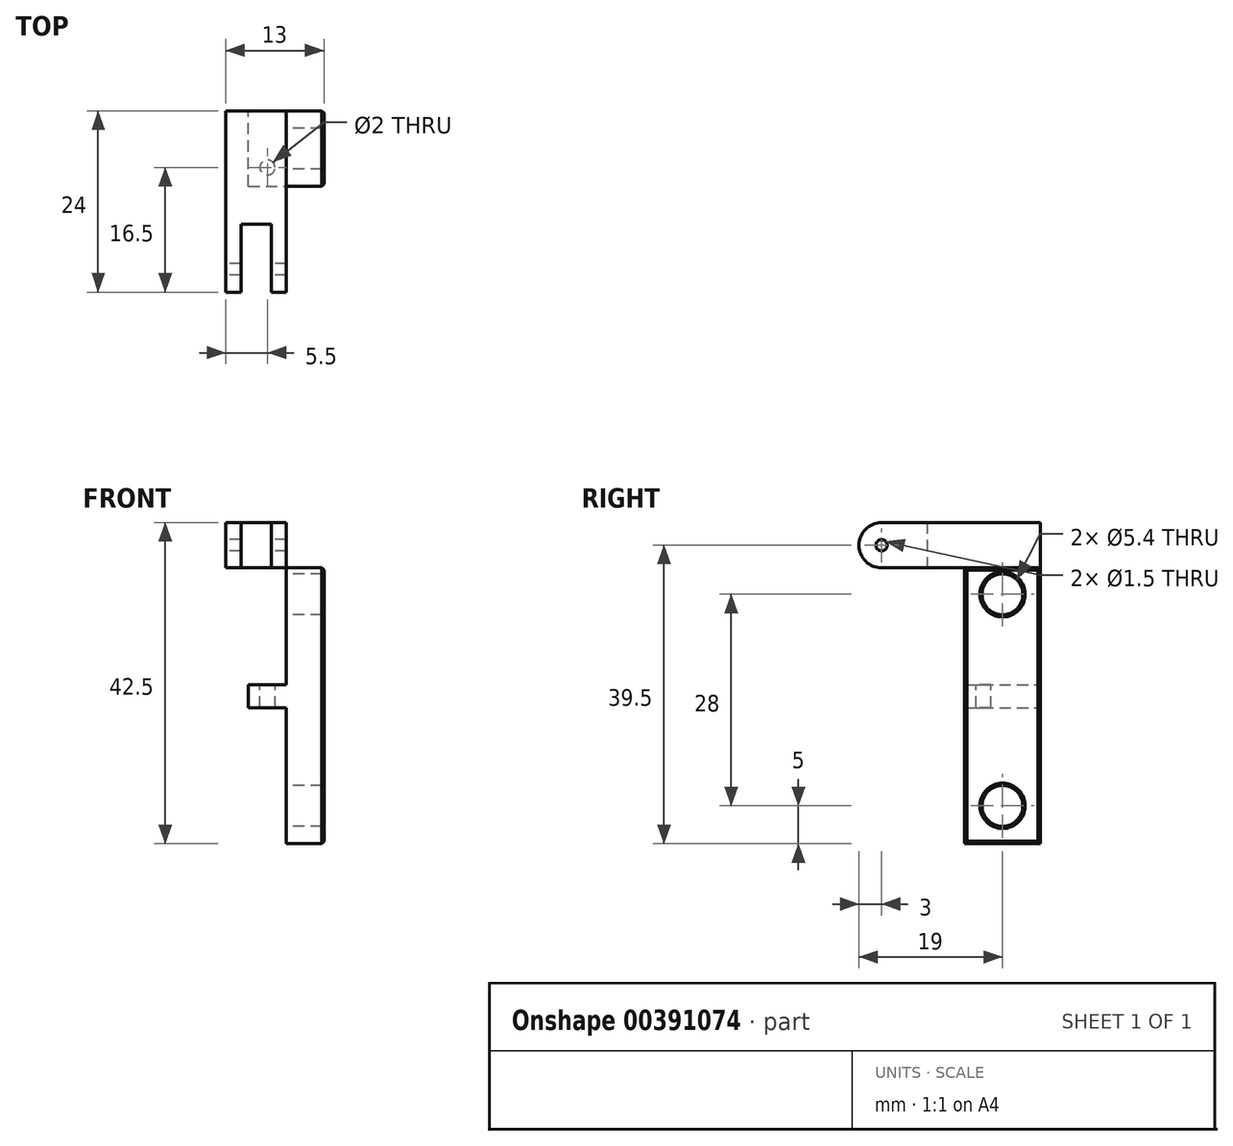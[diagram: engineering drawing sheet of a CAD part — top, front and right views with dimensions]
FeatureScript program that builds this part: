
annotation { "Feature Type Name" : "Feature", "Feature Type Description" : "" }
export const myFeature = defineFeature(function(context is Context, id is Id, definition is map)
    precondition{}
    {
        {
            var Q0;
            Q0=qCreatedBy(makeId("Front.planeOp"),FACE);
            var sketch = newSketch(context, id + "F0", { "sketchPlane" : qUnion([Q0])});
            skLineSegment(sketch, "E0.bottom", {"start": v(-13, 42.5) * mm, "end": v(0, 42.5) * mm});
            skLineSegment(sketch, "E0.top", {"start": v(-13, 36.5) * mm, "end": v(0, 36.5) * mm});
            skLineSegment(sketch, "E0.left", {"start": v(-13, 42.5) * mm, "end": v(-13, 36.5) * mm});
            skLineSegment(sketch, "E0.right", {"start": v(0, 42.5) * mm, "end": v(0, 36.5) * mm});
            skLineSegment(sketch, "E1.bottom", {"start": v(-5, 42.5) * mm, "end": v(0, 42.5) * mm});
            skLineSegment(sketch, "E1.top", {"start": v(-5, 0) * mm, "end": v(0, 0) * mm});
            skLineSegment(sketch, "E1.left", {"start": v(-5, 42.5) * mm, "end": v(-5, 21) * mm});
            skLineSegment(sketch, "E1.right", {"start": v(0, 42.5) * mm, "end": v(0, 0) * mm});
            skLineSegment(sketch, "E2.bottom", {"start": v(-10, 21) * mm, "end": v(-5, 21) * mm});
            skLineSegment(sketch, "E2.top", {"start": v(-10, 18) * mm, "end": v(-5, 18) * mm});
            skLineSegment(sketch, "E2.left", {"start": v(-10, 21) * mm, "end": v(-10, 18) * mm});
            skLineSegment(sketch, "E3.trimOffspring", {"start": v(-5, 18) * mm, "end": v(-5, 0) * mm});
            skPoint(sketch, "E4", {"position": v(-2.5, 5) * mm});
            skPoint(sketch, "E4.positionSnap0", {"position": v(-2.5, 0) * mm});
            skLineSegment(sketch, "E5", {"start": v(-11, 42.5) * mm, "end": v(-11, 36.5) * mm});
            skLineSegment(sketch, "E6", {"start": v(-7, 42.5) * mm, "end": v(-7, 36.5) * mm});
            skPoint(sketch, "E7", {"position": v(-2.5, 33) * mm});
            skSolve(sketch);
        }
        {
            var Q0;
            {var subQ0=sQuery(id+"F0.wireOp",EDGE,"E5");Q0=makeQuery(id+"F0.imprint","IMPRINT",FACE,{"disambiguationData":[TD([[makeQuery(id+"F0.imprint","IMPRINT",EDGE,{"derivedFrom":subQ0}),1.0]])]});}
            extrude(context, id + "F1", {"entities" : qUnion([Q0]), "depth" : 15 * mm, "offsetDistance" : 25 * mm});
        }
        {
            var Q0;
            {var subQ0=sQuery(id+"F0.wireOp",EDGE,"E0.left");Q0=makeQuery(id+"F0.imprint","IMPRINT",FACE,{"disambiguationData":[TD([[makeQuery(id+"F0.imprint","IMPRINT",EDGE,{"derivedFrom":subQ0}),1.0]])]});}
            var Q1;
            {var subQ3=sQuery(id+"F0.wireOp",EDGE,"E6");Q1=makeQuery(id+"F0.imprint","IMPRINT",FACE,{"disambiguationData":[TD([[makeQuery(id+"F0.imprint","IMPRINT",EDGE,{"derivedFrom":subQ3}),1.0]])]});}
            extrude(context, id + "F2", {"entities" : qUnion([Q0, Q1]), "operationType" : NewBodyOperationType.ADD, "depth" : 24 * mm, "offsetDistance" : 25 * mm});
        }
        {
            var Q0;
            {var subQ5=sQuery(id+"F0.wireOp",EDGE,"E1.bottom");Q0=makeQuery(id+"F0.imprint","IMPRINT",FACE,{"disambiguationData":[TD([[makeQuery(id+"F0.imprint","IMPRINT",EDGE,{"derivedFrom":subQ5}),-1.0]])]});}
            var Q1;
            {var subQ3=sQuery(id+"F0.wireOp",EDGE,"E1.top");Q1=makeQuery(id+"F0.imprint","IMPRINT",FACE,{"disambiguationData":[TD([[makeQuery(id+"F0.imprint","IMPRINT",EDGE,{"derivedFrom":subQ3}),1.0]])]});}
            extrude(context, id + "F3", {"entities" : qUnion([Q0, Q1]), "operationType" : NewBodyOperationType.ADD, "depth" : 10 * mm, "offsetDistance" : 25 * mm});
        }
        {
            var Q0;
            {var subQ0=sQuery(id+"F0.wireOp",EDGE,"E0.bottom");Q0=makeQuery(id+"F2.opExtrude","CAP_EDGE",EDGE,{"disambiguationData":[OSD([subQ0]),TDD([makeQuery(id+"F0.imprint","IMPRINT",EDGE,{"disambiguationData":[TD([[makeQuery(id+"F0.imprint","INTERSECT",VERTEX,{"derivedFrom":[subQ0,sQuery(id+"F0.wireOp",EDGE,"E6")]}),-1.0]])],"derivedFrom":subQ0})])],"isStart":false});}
            var Q1;
            {var subQ0=sQuery(id+"F0.wireOp",EDGE,"E0.top");Q1=makeQuery(id+"F2.opExtrude","CAP_EDGE",EDGE,{"disambiguationData":[OSD([subQ0]),TDD([makeQuery(id+"F0.imprint","IMPRINT",EDGE,{"disambiguationData":[TD([[makeQuery(id+"F0.imprint","INTERSECT",VERTEX,{"derivedFrom":[subQ0,sQuery(id+"F0.wireOp",EDGE,"E6")]}),-1.0]])],"derivedFrom":subQ0})])],"isStart":false});}
            var Q2;
            {var subQ0=sQuery(id+"F0.wireOp",EDGE,"E0.bottom");Q2=makeQuery(id+"F2.opExtrude","CAP_EDGE",EDGE,{"disambiguationData":[OSD([subQ0]),TDD([makeQuery(id+"F0.imprint","IMPRINT",EDGE,{"disambiguationData":[TD([[makeQuery(id+"F0.imprint","INTERSECT",VERTEX,{"derivedFrom":[subQ0,sQuery(id+"F0.wireOp",EDGE,"E0.left")]}),-1.0]])],"derivedFrom":subQ0})])],"isStart":false});}
            var Q3;
            {var subQ0=sQuery(id+"F0.wireOp",EDGE,"E0.top");Q3=makeQuery(id+"F2.opExtrude","CAP_EDGE",EDGE,{"disambiguationData":[OSD([subQ0]),TDD([makeQuery(id+"F0.imprint","IMPRINT",EDGE,{"disambiguationData":[TD([[makeQuery(id+"F0.imprint","INTERSECT",VERTEX,{"derivedFrom":[subQ0,sQuery(id+"F0.wireOp",EDGE,"E0.left")]}),-1.0]])],"derivedFrom":subQ0})])],"isStart":false});}
            fillet(context, id + "F4", {"entities" : qUnion([Q0, Q1, Q2, Q3]), "radius" : 3 * mm, "tangentPropagation" : true, "allowEdgeOverflow" : false});
        }
        {
            var Q0;
            Q0=makeQuery(id+"F2.opExtrude","SWEPT_FACE",FACE,{"disambiguationData":[OSD([sQuery(id+"F0.wireOp",EDGE,"E0.left")])]});
            var sketch = newSketch(context, id + "F5", { "sketchPlane" : qUnion([Q0])});
            skLineSegment(sketch, "E8.0.0", {"start": v(10, 21) * mm, "end": v(10, 36.5) * mm});
            skLineSegment(sketch, "E8.0.1", {"start": v(10, 36.5) * mm, "end": v(0, 36.5) * mm});
            skLineSegment(sketch, "E8.0.2", {"start": v(0, 36.5) * mm, "end": v(0, 21) * mm});
            skLineSegment(sketch, "E8.0.3", {"start": v(0, 21) * mm, "end": v(10, 21) * mm});
            skLineSegment(sketch, "E9.0.0", {"start": v(0, 18) * mm, "end": v(0, 0) * mm});
            skLineSegment(sketch, "E9.0.1", {"start": v(0, 0) * mm, "end": v(10, 0) * mm});
            skLineSegment(sketch, "E9.0.2", {"start": v(10, 0) * mm, "end": v(10, 18) * mm});
            skLineSegment(sketch, "E9.0.3", {"start": v(10, 18) * mm, "end": v(0, 18) * mm});
            skLineSegment(sketch, "E10.0.0", {"start": v(0, 21) * mm, "end": v(0, 18) * mm});
            skLineSegment(sketch, "E10.0.1", {"start": v(0, 18) * mm, "end": v(10, 18) * mm});
            skLineSegment(sketch, "E10.0.2", {"start": v(10, 18) * mm, "end": v(10, 21) * mm});
            skLineSegment(sketch, "E10.0.3", {"start": v(10, 21) * mm, "end": v(0, 21) * mm});
            skLineSegment(sketch, "E11.0.1", {"start": v(0, 42.5) * mm, "end": v(0, 36.5) * mm});
            skLineSegment(sketch, "E11.0.3", {"start": v(0, 36.5) * mm, "end": v(0, 42.5) * mm});
            skLineSegment(sketch, "E11.1.0", {"start": v(0, 36.5) * mm, "end": v(0, 42.5) * mm});
            skLineSegment(sketch, "E11.1.2", {"start": v(0, 42.5) * mm, "end": v(0, 36.5) * mm});
            skLineSegment(sketch, "E12.0", {"start": v(21, 42.5) * mm, "end": v(0, 42.5) * mm});
            skArc(sketch, "E13.0", {"start": v(21, 36.5) * mm, "mid": v(24, 39.5) * mm, "end": v(21, 42.5) * mm});
            skLineSegment(sketch, "E14.0", {"start": v(21, 36.5) * mm, "end": v(0, 36.5) * mm});
            skPoint(sketch, "E15", {"position": v(5, 33) * mm});
            skPoint(sketch, "E15.positionSnap0", {"position": v(5, 36.5) * mm});
            skPoint(sketch, "E16", {"position": v(5, 5) * mm});
            skPoint(sketch, "E16.positionSnap0", {"position": v(5, 0) * mm});
            skCircle(sketch, "E17", {"center": v(5, 33) * mm, "radius": 2.7 * mm});
            skCircle(sketch, "E18", {"center": v(5, 5) * mm, "radius": 2.7 * mm});
            skCircle(sketch, "E19", {"center": v(21, 39.5) * mm, "radius": 0.75 * mm});
            skSolve(sketch);
        }
        {
            var Q0;
            Q0=makeQuery(id+"F5.imprint","IMPRINT",FACE,{"disambiguationData":[TD([[makeQuery(id+"F5.imprint","IMPRINT",EDGE,{"derivedFrom":sQuery(id+"F5.wireOp",EDGE,"E17")}),1.0]])]});
            var Q1;
            Q1=makeQuery(id+"F5.imprint","IMPRINT",FACE,{"disambiguationData":[TD([[makeQuery(id+"F5.imprint","IMPRINT",EDGE,{"derivedFrom":sQuery(id+"F5.wireOp",EDGE,"E18")}),1.0]])]});
            var Q2;
            Q2=makeQuery(id+"F5.imprint","IMPRINT",FACE,{"disambiguationData":[TD([[makeQuery(id+"F5.imprint","IMPRINT",EDGE,{"derivedFrom":sQuery(id+"F5.wireOp",EDGE,"E19")}),1.0]])]});
            extrude(context, id + "F6", {"entities" : qUnion([Q0, Q1, Q2]), "operationType" : NewBodyOperationType.REMOVE, "endBound" : BoundingType.THROUGH_ALL, "oppositeDirection" : true, "depth" : 25 * mm, "offsetDistance" : 25 * mm});
        }
        {
            var Q0;
            Q0=sQuery(id+"F0.wireOp",VERTEX,"E7");
            var Q1;
            Q1=sQuery(id+"F0.wireOp",VERTEX,"E4");
            var Q2;
            Q2=makeQuery(id+"F1.opExtrude","SWEPT_BODY",BODY,{"disambiguationData":[OSD([sQuery(id+"F0.wireOp",EDGE,"E0.bottom"),sQuery(id+"F0.wireOp",EDGE,"E0.top"),sQuery(id+"F0.wireOp",EDGE,"E5"),sQuery(id+"F0.wireOp",EDGE,"E6")])]});
            hole(context, id + "F7", {"style" : HoleStyle.SIMPLE, "endStyle" : HoleEndStyle.BLIND, "oppositeDirection" : true, "holeDiameter" : 1.1 * mm, "majorDiameter" : 5 * mm, "holeDepth" : 40 * mm, "isTappedThrough" : true, "tappedDepth" : 100 * mm, "tapClearance" : 3, "startFromSketch" : true, "locations" : qUnion([Q0, Q1]), "scope" : qUnion([Q2])});
        }
        {
            var Q0;
            Q0=makeQuery(id+"F3.opExtrude","SWEPT_FACE",FACE,{"disambiguationData":[OSD([sQuery(id+"F0.wireOp",EDGE,"E2.bottom")])]});
            var sketch = newSketch(context, id + "F8", { "sketchPlane" : qUnion([Q0])});
            skLineSegment(sketch, "E20.0", {"start": v(0, -10) * mm, "end": v(0, 0) * mm});
            skPoint(sketch, "E20.1", {"position": v(0, -5) * mm});
            skPoint(sketch, "E21", {"position": v(-7.5, -7.5) * mm});
            skCircle(sketch, "E22", {"center": v(-7.5, -7.5) * mm, "radius": 1 * mm});
            skSolve(sketch);
        }
        {
            var Q0;
            Q0=makeQuery(id+"F8.imprint","IMPRINT",FACE,{"disambiguationData":[TD([[makeQuery(id+"F8.imprint","IMPRINT",EDGE,{"derivedFrom":sQuery(id+"F8.wireOp",EDGE,"E22")}),1.0]])]});
            extrude(context, id + "F9", {"entities" : qUnion([Q0]), "operationType" : NewBodyOperationType.REMOVE, "endBound" : BoundingType.THROUGH_ALL, "oppositeDirection" : true, "depth" : 25 * mm, "offsetDistance" : 25 * mm});
        }
        {
            var Q0;
            Q0=makeQuery(id+"F3.opExtrude","SWEPT_FACE",FACE,{"disambiguationData":[OSD([sQuery(id+"F0.wireOp",EDGE,"E1.right")])]});
            chamfer(context, id + "F10", {"entities" : qUnion([Q0]), "width" : .3 * mm, "tangentPropagation" : true});
        }
    });
